# Revit family: Haworth_Typical_Parametric_Compose_L_Corner90Degree
name_source: partatom
category: Furniture Systems
revit_build: Autodesk Revit Architecture 2014 (Build: 20130308_1515(x64)
units: mm (PartAtom-declared; Revit-internal decimal feet)

## types (2) — shared parameters
Actual Off Spine Height = 50"
Actual Spine Height = 66"
Actual Wing Height = 50"
Actual Wing Length = 24"
Actual Worksurface Depth = 24"
Assembly Code = E2020200
Box Box File = Yes
Box Box File Offset = 1/4"
Classic Pull = No
Crescent Pull = No
Description = Haworth_Typical_Parametric_Compose_L_Corner90Degree
File Cabinet Finish = Haworth _ Paint _ Smoke
File Depth = 23"
File Drawer Finish = Haworth _ Paint _ Smoke
File Pull Finish = Haworth _ Metal _ Brushed Aluminum
Glass Stack Finish = Haworth _ Glass _ Clear
Glass Stack Height = 16"
Glass Stack Panel = Yes
Hardware Finish = Haworth _ Metal _ Brushed Aluminum
J Pull = No
Linear Pull = Yes
Manufacturer = Haworth
Max Height = 74"
Max Length = 108"
Max Worksurface Depth = 30"
Maximum Length = 108 in.
Min Height = 34"
Min Length = 60"
Min Length Wing = 24"
Min Worksurface Depth = 18"
Minimum Length = 60 in.
Model = Haworth_Typical_Parametric_Compose_L_Corner90Degree
Multiple Panel Tiles = Yes
Off Spine End Cap = No
Off Spine End Panel = No
Off Spine Height = 50"
Off Spine Tile Count = 2
Overhead Storage Door Finish = Haworth _ Fabric _ Striae _ Band C1-AM
Overhead Storage Frame Finish = Haworth _ Metal _ Brushed Aluminum
Overhead Storage Inside = Yes
Overhead Storage Inside Actual = Yes
Overhead Storage Mounting Height = 50"
Overhead Storage Outside = Yes
Overhead Storage Outside Actual = Yes
Panel High Tile Finish = Haworth _ Fabric _ Striae _ Band C1-AM
Panel Low Tile Finish = Haworth _ Fabric _ Striae _ Beam C1-AJ
Panel Thickness Half = 1 1/2"
Radius Pull = No
Revision = 1
Seat Arm Cap Finish = Haworth _ Paint _ Smoke
Seat Back Upholstery Finish = Haworth _ Fabric _ Zody Mesh _ Comfort MA-002
Seat Cushion Finish = Haworth _ Fabric _ Zinger _ Gravel NI-4
Seat Shell Finish = Haworth _ Metal _ Brushed Aluminum
Seat Support Finish = Haworth _ Paint _ Smoke
Single Panel Tile = No
Size = Verify Final Dim. w/ Haworth
Spine Height = 66"
Spine Tile Count = 3
Standard Panel Heights = 34, 42, 50, 58, 66, 74 in.
Sustainability Info = www.haworth.com/en-us/About-Us/Sustainability/Pages/Vision.aspx
Task Chair = Yes
URL = http://haworth.com
URL - Product = http://haworth.com
Warranty = http://haworth.com
Wing Height = 50"
Wing Length = 24"
Wing Panel = Yes
Wing Tile Count = 2
Worksurface Depth = 24"
Worksurface Edge Finish = Haworth _ Laminate _ Linen H-WL
Worksurface Finish = Haworth _ Laminate _ Linen H-WL

## per-type parameters (varying)
| type | Actual Off Spine Length | Actual Spine Length | Combo File | Corner Length | Enclosure Glass Stack | Enclosure Panels | File File | File File Actual | File Offset | Max Length Wing | Off Spine Length | Off Spine Straight Surface Length | Spine End Cap | Spine End Panel | Spine Length | Spine Straight Surface Length |
| 8x8 | 96" | 96" | Yes | 48" | No | No | No | No | 1 1/2" | 60" | 96" | 48" | Yes | Yes | 96" | 48" |
| 6x6 | 72" | 72" | No | 36" | Yes | Yes | Yes | Yes | 1/4" | 36" | 72" | 36" | No | No | 72" | 36" |

## geometry (parser evidence)
native form markers: Blend x36, Sweep x80
no freeform markers — native parametric forms only
